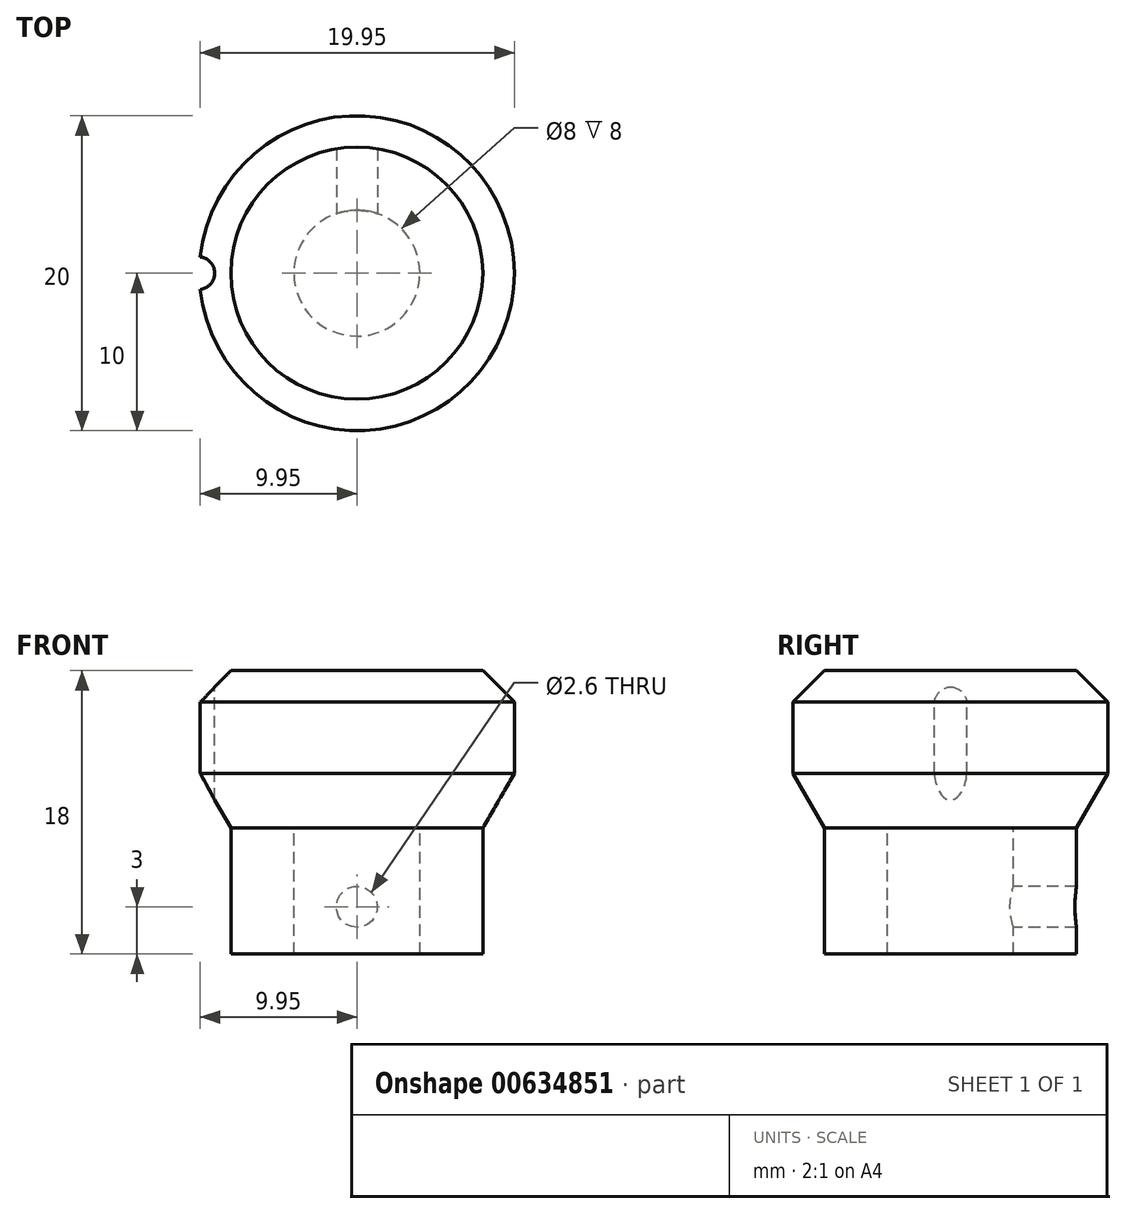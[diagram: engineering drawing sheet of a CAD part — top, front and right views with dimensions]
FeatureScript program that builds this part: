
annotation { "Feature Type Name" : "Feature", "Feature Type Description" : "" }
export const myFeature = defineFeature(function(context is Context, id is Id, definition is map)
    precondition{}
    {
        {
            var Q0;
            Q0=qCreatedBy(makeId("Front.planeOp"),FACE);
            var sketch = newSketch(context, id + "F0", { "sketchPlane" : qUnion([Q0])});
            skLineSegment(sketch, "E0", {"start": v(0, 0) * mm, "end": v(-4, 0) * mm});
            skLineSegment(sketch, "E1", {"start": v(-4, 0) * mm, "end": v(-4, -8) * mm});
            skLineSegment(sketch, "E2", {"start": v(-4, -8) * mm, "end": v(-8, -8) * mm});
            skLineSegment(sketch, "E3", {"start": v(-8, -8) * mm, "end": v(-8, 0) * mm});
            skLineSegment(sketch, "E4", {"start": v(-8, 0) * mm, "end": v(-10, 3.46) * mm});
            skLineSegment(sketch, "E5", {"start": v(-10, 3.46) * mm, "end": v(-10, 10) * mm});
            skLineSegment(sketch, "E6", {"start": v(-10, 10) * mm, "end": v(0, 10) * mm});
            skLineSegment(sketch, "E7", {"start": v(0, 10) * mm, "end": v(0, 0) * mm});
            skSolve(sketch);
        }
        {
            var Q0;
            Q0=makeQuery(id+"F0.imprint","IMPRINT",FACE,{"disambiguationData":[TD([[makeQuery(id+"F0.imprint","IMPRINT",EDGE,{"derivedFrom":sQuery(id+"F0.wireOp",EDGE,"E0")}),-1.0]])]});
            var Q1;
            Q1=sQuery(id+"F0.wireOp",EDGE,"E7");
            revolve(context, id + "F1", {"entities" : qUnion([Q0]), "axis" : qUnion([Q1]), "revolveType" : RevolveType.FULL});
        }
        {
            var Q0;
            Q0=makeQuery(id+"F1.opRevolve","SWEPT_EDGE",EDGE,{"disambiguationData":[OSD([sQuery(id+"F0.wireOp",EDGE,"E5"),sQuery(id+"F0.wireOp",EDGE,"E6")])]});
            chamfer(context, id + "F2", {"entities" : qUnion([Q0]), "width" : 2 * mm, "tangentPropagation" : true});
        }
        {
            var Q0;
            Q0=makeQuery(id+"F1.opRevolve","SWEPT_FACE",FACE,{"disambiguationData":[OSD([sQuery(id+"F0.wireOp",EDGE,"E6")])]});
            var sketch = newSketch(context, id + "F3", { "sketchPlane" : qUnion([Q0])});
            skCircle(sketch, "E8", {"center": v(-10.08, 0) * mm, "radius": 1.04 * mm});
            skSolve(sketch);
        }
        {
            var Q0;
            Q0=makeQuery(id+"F3.imprint","IMPRINT",FACE,{"disambiguationData":[TD([[makeQuery(id+"F3.imprint","IMPRINT",EDGE,{"derivedFrom":sQuery(id+"F3.wireOp",EDGE,"E8")}),1.0]])]});
            extrude(context, id + "F4", {"entities" : qUnion([Q0]), "operationType" : NewBodyOperationType.REMOVE, "oppositeDirection" : true, "depth" : 25 * mm, "offsetDistance" : 25 * mm});
        }
        {
            var Q0;
            Q0=qCreatedBy(makeId("Front.planeOp"),FACE);
            var sketch = newSketch(context, id + "F5", { "sketchPlane" : qUnion([Q0])});
            skPoint(sketch, "E9", {"position": v(0, -5) * mm});
            skSolve(sketch);
        }
        {
            var Q0;
            Q0=sQuery(id+"F5.wireOp",VERTEX,"E9");
            var Q1;
            Q1=makeQuery(id+"F1.opRevolve","SWEPT_BODY",BODY,{"disambiguationData":[OSD([sQuery(id+"F0.wireOp",EDGE,"E0"),sQuery(id+"F0.wireOp",EDGE,"E1"),sQuery(id+"F0.wireOp",EDGE,"E2"),sQuery(id+"F0.wireOp",EDGE,"E3"),sQuery(id+"F0.wireOp",EDGE,"E4"),sQuery(id+"F0.wireOp",EDGE,"E5"),sQuery(id+"F0.wireOp",EDGE,"E6"),sQuery(id+"F0.wireOp",EDGE,"E7")])]});
            hole(context, id + "F6", {"style" : HoleStyle.SIMPLE, "endStyle" : HoleEndStyle.THROUGH, "holeDiameter" : 2.6 * mm, "majorDiameter" : 5 * mm, "isTappedThrough" : true, "tappedDepth" : 15 * mm, "tapClearance" : 0, "startFromSketch" : true, "locations" : qUnion([Q0]), "scope" : qUnion([Q1])});
        }
    });
